# Revit family: Table-Teknion-Zones_ZNTCD-R2013
name_source: partatom
category: Furniture
revit_build: Autodesk Revit 2013 (Build: 20130531_2115(x64)
units: mm (PartAtom-declared; Revit-internal decimal feet)

## types (4) — shared parameters
Apparent Load = 0 VA
Assembly Code = E2020200
Height = 43 1/2"
Manufacturer = Teknion
Manufacturer Fax = 416.661.4586
Part Number = ZNTCD
Product Documentation Link = http://www.teknion.com
Product Line = Zones
Product Page URL = http://www.teknion.com
Series = Zones
Sustainability Data = http://www.teknion.com
URL = www.teknion.com
Unit Weight URL = http://www.teknion.com
Warranty = http://www.teknion.com
Width = 72"

## per-type parameters (varying)
| type | Connector Description | Depth | Description | Model | Power Pill Cutout | Power Trim Offset | Voltage |
| 30" x 72" Without Power Pill | Without Power Connector | 30" | Dynamic Cubby Table, 30"d x 72"w, No Cut-Out | ZNTCD3072N | No | 80" | 0 V |
| 36" x 72" Without Power Pill | Without Power Connector | 36" | Dynamic Cubby Table, 36"d x 72"w, No Cut-Out | ZNTCD3672N | No | 80" | 0 V |
| 36" x 72"  With Power Pill | Power Connector | 36" | Dynamic Cubby Table, 36"d x 72"w, One Center Cut-Out | ZNTCD3672Y | Yes | 36" | 120 V |
| 30" x 72" With Power Pill | Power Connector | 30" | Dynamic Cubby Table, 30"d x 72"w, One Center Cut-Out | ZNTCD3072Y | Yes | 36" | 120 V |

## geometry (parser evidence)
native form markers: Blend x6, Sweep x7
no freeform markers — native parametric forms only
